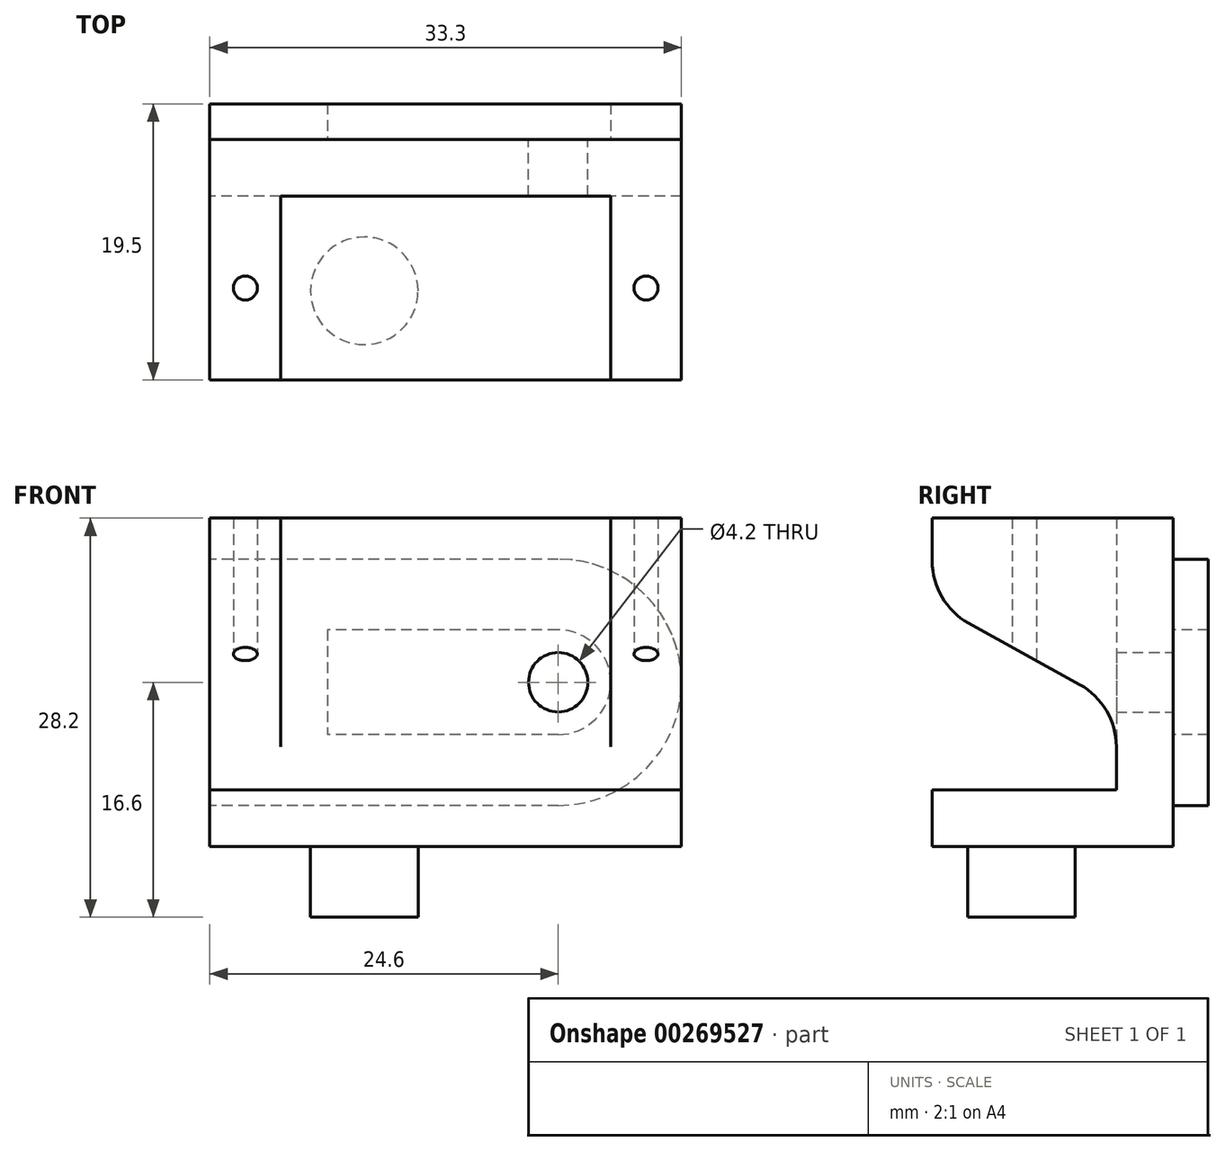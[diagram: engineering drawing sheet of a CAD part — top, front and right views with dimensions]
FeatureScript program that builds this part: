
annotation { "Feature Type Name" : "Feature", "Feature Type Description" : "" }
export const myFeature = defineFeature(function(context is Context, id is Id, definition is map)
    precondition{}
    {
        {
            var Q0;
            Q0=qCreatedBy(makeId("Top.planeOp"),FACE);
            var sketch = newSketch(context, id + "F0", { "sketchPlane" : qUnion([Q0])});
            skLineSegment(sketch, "E0.bottom", {"start": v(16.65, 8.5) * mm, "end": v(-16.65, 8.5) * mm});
            skLineSegment(sketch, "E0.top", {"start": v(16.65, -8.5) * mm, "end": v(-16.65, -8.5) * mm});
            skLineSegment(sketch, "E0.left", {"start": v(16.65, 8.5) * mm, "end": v(16.65, -8.5) * mm});
            skLineSegment(sketch, "E0.right", {"start": v(-16.65, 8.5) * mm, "end": v(-16.65, -8.5) * mm});
            skPoint(sketch, "E0.middle", {"position": v(0, 0) * mm});
            skLineSegment(sketch, "E1", {"start": v(11.65, -8.5) * mm, "end": v(11.65, 8.5) * mm});
            skLineSegment(sketch, "E2", {"start": v(-11.65, -8.5) * mm, "end": v(-11.65, 8.5) * mm});
            skLineSegment(sketch, "E3", {"start": v(-11.65, 4.5) * mm, "end": v(11.65, 4.5) * mm});
            skCircle(sketch, "E4", {"center": v(14.15, -2) * mm, "radius": 0.85 * mm});
            skCircle(sketch, "E5", {"center": v(-14.15, -2) * mm, "radius": 0.85 * mm});
            skCircle(sketch, "E6", {"center": v(-5.75, -2.2) * mm, "radius": 3.8 * mm});
            skCircle(sketch, "E7.MirrorC", {"center": v(5.75, -2.2) * mm, "radius": 3.8 * mm});
            skSolve(sketch);
        }
        {
            var Q0;
            Q0=qCreatedBy(makeId("Front.planeOp"),FACE);
            var sketch = newSketch(context, id + "F1", { "sketchPlane" : qUnion([Q0])});
            skLineSegment(sketch, "E8.bottom", {"start": v(-16.65, 0) * mm, "end": v(16.65, 0) * mm});
            skLineSegment(sketch, "E8.top", {"start": v(-16.65, 23.2) * mm, "end": v(16.65, 23.2) * mm});
            skLineSegment(sketch, "E8.left", {"start": v(-16.65, 0) * mm, "end": v(-16.65, 23.2) * mm});
            skLineSegment(sketch, "E8.right", {"start": v(16.65, 0) * mm, "end": v(16.65, 23.2) * mm});
            skLineSegment(sketch, "E9", {"start": v(-16.65, 4) * mm, "end": v(16.65, 4) * mm});
            skLineSegment(sketch, "E10", {"start": v(11.65, 0) * mm, "end": v(11.65, 23.2) * mm});
            skLineSegment(sketch, "E11", {"start": v(-11.65, 0) * mm, "end": v(-11.65, 23.2) * mm});
            skLineSegment(sketch, "E12", {"start": v(16.65, 10) * mm, "end": v(11.65, 10) * mm});
            skLineSegment(sketch, "E13", {"start": v(-11.65, 10) * mm, "end": v(-16.65, 10) * mm});
            skLineSegment(sketch, "E14", {"start": v(11.65, 17.2) * mm, "end": v(16.65, 17.2) * mm});
            skLineSegment(sketch, "E15", {"start": v(-11.65, 17.2) * mm, "end": v(-16.65, 17.2) * mm});
            skSolve(sketch);
        }
        {
            var Q0;
            Q0=qCreatedBy(makeId("Right.planeOp"),FACE);
            var sketch = newSketch(context, id + "F2", { "sketchPlane" : qUnion([Q0])});
            skLineSegment(sketch, "E16.bottom", {"start": v(-8.5, 0) * mm, "end": v(8.5, 0) * mm});
            skLineSegment(sketch, "E16.top", {"start": v(-8.5, 23.2) * mm, "end": v(8.5, 23.2) * mm});
            skLineSegment(sketch, "E16.left", {"start": v(-8.5, 20.15) * mm, "end": v(-8.5, 23.2) * mm});
            skLineSegment(sketch, "E16.right", {"start": v(8.5, 0) * mm, "end": v(8.5, 23.2) * mm});
            skLineSegment(sketch, "E17", {"start": v(4.5, 7.05) * mm, "end": v(4.5, 0) * mm});
            skLineSegment(sketch, "E18", {"start": v(4.5, 17.2) * mm, "end": v(-8.5, 17.2) * mm});
            skLineSegment(sketch, "E19", {"start": v(4.5, 4) * mm, "end": v(-8.5, 4) * mm});
            skLineSegment(sketch, "E20", {"start": v(-8.5, 10) * mm, "end": v(4.5, 10) * mm});
            skLineSegment(sketch, "E21", {"start": v(-5.92, 15.77) * mm, "end": v(1.92, 11.43) * mm});
            skArc(sketch, "E22.filletArc", {"start": v(-8.5, 20.15) * mm, "mid": v(-7.8, 17.6) * mm, "end": v(-5.92, 15.77) * mm});
            skArc(sketch, "E23.filletArc", {"start": v(4.5, 7.05) * mm, "mid": v(3.8, 9.6) * mm, "end": v(1.92, 11.43) * mm});
            skLineSegment(sketch, "E24", {"start": v(-8.5, 20.15) * mm, "end": v(-8.5, 0) * mm});
            skSolve(sketch);
        }
        {
            var Q0;
            {var subQ0=sQuery(id+"F1.wireOp",EDGE,"E13");Q0=makeQuery(id+"F1.imprint","IMPRINT",FACE,{"disambiguationData":[TD([[makeQuery(id+"F1.imprint","IMPRINT",EDGE,{"derivedFrom":subQ0}),-1.0]])]});}
            var Q1;
            {var subQ5=sQuery(id+"F1.wireOp",EDGE,"E15");Q1=makeQuery(id+"F1.imprint","IMPRINT",FACE,{"disambiguationData":[TD([[makeQuery(id+"F1.imprint","IMPRINT",EDGE,{"derivedFrom":subQ5}),-1.0]])]});}
            var Q2;
            {var subQ3=sQuery(id+"F1.wireOp",EDGE,"E13");Q2=makeQuery(id+"F1.imprint","IMPRINT",FACE,{"disambiguationData":[TD([[makeQuery(id+"F1.imprint","IMPRINT",EDGE,{"derivedFrom":subQ3}),1.0]])]});}
            var Q3;
            {var subQ0=sQuery(id+"F1.wireOp",EDGE,"E8.left");var subQ1=sQuery(id+"F1.wireOp",EDGE,"E8.bottom");var subQ2=makeQuery(id+"F1.imprint","INTERSECT",VERTEX,{"derivedFrom":[subQ1,subQ0]});Q3=makeQuery(id+"F1.imprint","IMPRINT",FACE,{"disambiguationData":[TD([[makeQuery(id+"F1.imprint","IMPRINT",EDGE,{"disambiguationData":[TD([[subQ2,-1.0]])],"derivedFrom":subQ1}),1.0]])]});}
            var Q4;
            {var subQ0=sQuery(id+"F1.wireOp",EDGE,"E10");var subQ1=sQuery(id+"F1.wireOp",EDGE,"E8.bottom");var subQ2=makeQuery(id+"F1.imprint","INTERSECT",VERTEX,{"derivedFrom":[subQ1,subQ0]});Q4=makeQuery(id+"F1.imprint","IMPRINT",FACE,{"disambiguationData":[TD([[makeQuery(id+"F1.imprint","IMPRINT",EDGE,{"disambiguationData":[TD([[subQ2,1.0]])],"derivedFrom":subQ1}),1.0]])]});}
            var Q5;
            {var subQ0=sQuery(id+"F1.wireOp",EDGE,"E8.right");var subQ1=sQuery(id+"F1.wireOp",EDGE,"E8.bottom");var subQ2=makeQuery(id+"F1.imprint","INTERSECT",VERTEX,{"derivedFrom":[subQ1,subQ0]});Q5=makeQuery(id+"F1.imprint","IMPRINT",FACE,{"disambiguationData":[TD([[makeQuery(id+"F1.imprint","IMPRINT",EDGE,{"disambiguationData":[TD([[subQ2,1.0]])],"derivedFrom":subQ1}),1.0]])]});}
            var Q6;
            {var subQ3=sQuery(id+"F1.wireOp",EDGE,"E12");Q6=makeQuery(id+"F1.imprint","IMPRINT",FACE,{"disambiguationData":[TD([[makeQuery(id+"F1.imprint","IMPRINT",EDGE,{"derivedFrom":subQ3}),1.0]])]});}
            var Q7;
            {var subQ0=sQuery(id+"F1.wireOp",EDGE,"E12");Q7=makeQuery(id+"F1.imprint","IMPRINT",FACE,{"disambiguationData":[TD([[makeQuery(id+"F1.imprint","IMPRINT",EDGE,{"derivedFrom":subQ0}),-1.0]])]});}
            var Q8;
            {var subQ5=sQuery(id+"F1.wireOp",EDGE,"E14");Q8=makeQuery(id+"F1.imprint","IMPRINT",FACE,{"disambiguationData":[TD([[makeQuery(id+"F1.imprint","IMPRINT",EDGE,{"derivedFrom":subQ5}),1.0]])]});}
            extrude(context, id + "F3", {"entities" : qUnion([Q0, Q1, Q2, Q3, Q4, Q5, Q6, Q7, Q8]), "endBound" : BoundingType.SYMMETRIC, "depth" : 17 * mm});
        }
        {
            var Q0;
            {var subQ5=sQuery(id+"F0.wireOp",EDGE,"E3");Q0=makeQuery(id+"F0.imprint","IMPRINT",FACE,{"disambiguationData":[TD([[makeQuery(id+"F0.imprint","IMPRINT",EDGE,{"derivedFrom":subQ5}),1.0]])]});}
            extrude(context, id + "F4", {"entities" : qUnion([Q0]), "operationType" : NewBodyOperationType.ADD, "depth" : 23.2 * mm});
        }
        {
            var Q0;
            {var subQ0=sQuery(id+"F2.wireOp",EDGE,"E21");Q0=makeQuery(id+"F2.imprint","IMPRINT",FACE,{"disambiguationData":[TD([[makeQuery(id+"F2.imprint","IMPRINT",EDGE,{"derivedFrom":subQ0}),-1.0]])]});}
            var Q1;
            {var subQ0=sQuery(id+"F2.wireOp",EDGE,"E24");var subQ1=sQuery(id+"F2.wireOp",EDGE,"E18");var subQ2=makeQuery(id+"F2.imprint","INTERSECT",VERTEX,{"derivedFrom":[subQ1,subQ0]});Q1=makeQuery(id+"F2.imprint","IMPRINT",FACE,{"disambiguationData":[TD([[makeQuery(id+"F2.imprint","IMPRINT",EDGE,{"disambiguationData":[TD([[subQ2,1.0]])],"derivedFrom":subQ1}),-1.0]])]});}
            var Q2;
            {var subQ5=sQuery(id+"F2.wireOp",EDGE,"E19");Q2=makeQuery(id+"F2.imprint","IMPRINT",FACE,{"disambiguationData":[TD([[makeQuery(id+"F2.imprint","IMPRINT",EDGE,{"derivedFrom":subQ5}),-1.0]])]});}
            extrude(context, id + "F5", {"entities" : qUnion([Q0, Q1, Q2]), "operationType" : NewBodyOperationType.REMOVE, "endBound" : BoundingType.SYMMETRIC, "oppositeDirection" : true, "depth" : 36.2 * mm});
        }
        {
            var Q0;
            Q0=makeQuery(id+"F0.imprint","IMPRINT",FACE,{"disambiguationData":[TD([[makeQuery(id+"F0.imprint","IMPRINT",EDGE,{"derivedFrom":sQuery(id+"F0.wireOp",EDGE,"E4")}),1.0]])]});
            var Q1;
            Q1=makeQuery(id+"F0.imprint","IMPRINT",FACE,{"disambiguationData":[TD([[makeQuery(id+"F0.imprint","IMPRINT",EDGE,{"derivedFrom":sQuery(id+"F0.wireOp",EDGE,"E5")}),1.0]])]});
            extrude(context, id + "F6", {"entities" : qUnion([Q0, Q1]), "operationType" : NewBodyOperationType.REMOVE, "depth" : 25 * mm, "hasSecondDirection" : true, "secondDirectionOppositeDirection" : false, "secondDirectionDepth" : 4.3 * mm});
        }
        {
            var Q0;
            Q0=makeQuery(id+"F0.imprint","IMPRINT",FACE,{"disambiguationData":[TD([[makeQuery(id+"F0.imprint","IMPRINT",EDGE,{"derivedFrom":sQuery(id+"F0.wireOp",EDGE,"E6")}),1.0]])]});
            extrude(context, id + "F7", {"entities" : qUnion([Q0]), "operationType" : NewBodyOperationType.ADD, "oppositeDirection" : true, "depth" : 5 * mm, "offsetDistance" : 25 * mm});
        }
        {
            var Q0;
            Q0=makeQuery(id+"F4.boolean.opBoolean","MERGE",FACE,{"derivedFrom":[makeQuery(id+"F3.opExtrude","CAP_FACE",FACE,{"disambiguationData":[OSD([sQuery(id+"F1.wireOp",EDGE,"E8.bottom"),sQuery(id+"F1.wireOp",EDGE,"E8.top"),sQuery(id+"F1.wireOp",EDGE,"E8.left"),sQuery(id+"F1.wireOp",EDGE,"E8.right"),sQuery(id+"F1.wireOp",EDGE,"E9"),sQuery(id+"F1.wireOp",EDGE,"E10"),sQuery(id+"F1.wireOp",EDGE,"E11")])],"isStart":true}),makeQuery(id+"F4.opExtrude","SWEPT_FACE",FACE,{"disambiguationData":[OSD([sQuery(id+"F0.wireOp",EDGE,"E0.bottom")])]})]});
            var sketch = newSketch(context, id + "F8", { "sketchPlane" : qUnion([Q0])});
            skLineSegment(sketch, "E25.bottom", {"start": v(-16.65, 0) * mm, "end": v(16.65, 0) * mm});
            skLineSegment(sketch, "E25.top", {"start": v(-16.65, 23.2) * mm, "end": v(16.65, 23.2) * mm});
            skLineSegment(sketch, "E25.left", {"start": v(-16.65, 0) * mm, "end": v(-16.65, 23.2) * mm});
            skLineSegment(sketch, "E25.right", {"start": v(16.65, 0) * mm, "end": v(16.65, 23.2) * mm});
            skCircle(sketch, "E26", {"center": v(-7.95, 11.6) * mm, "radius": 2.1 * mm});
            skCircle(sketch, "E27", {"center": v(-7.95, 11.6) * mm, "radius": 3.7 * mm});
            skLineSegment(sketch, "E28.bottom", {"start": v(-7.95, 15.3) * mm, "end": v(8.35, 15.3) * mm});
            skLineSegment(sketch, "E28.top", {"start": v(-7.95, 7.9) * mm, "end": v(8.35, 7.9) * mm});
            skLineSegment(sketch, "E28.left", {"start": v(-7.95, 15.3) * mm, "end": v(-7.95, 7.9) * mm});
            skLineSegment(sketch, "E28.right", {"start": v(8.35, 15.3) * mm, "end": v(8.35, 7.9) * mm});
            skCircle(sketch, "E29", {"center": v(-7.95, 11.6) * mm, "radius": 8.7 * mm});
            skLineSegment(sketch, "E30", {"start": v(-7.95, 20.3) * mm, "end": v(16.65, 20.3) * mm});
            skLineSegment(sketch, "E31", {"start": v(-7.95, 2.9) * mm, "end": v(16.65, 2.9) * mm});
            skSolve(sketch);
        }
        {
            var Q0;
            {var subQ4=sQuery(id+"F8.wireOp",EDGE,"E29");var subQ10=makeQuery(id+"F8.imprint","INTERSECT",VERTEX,{"derivedFrom":[subQ4,sQuery(id+"F8.wireOp",EDGE,"E30")]});Q0=makeQuery(id+"F8.imprint","IMPRINT",FACE,{"disambiguationData":[TD([[makeQuery(id+"F8.imprint","IMPRINT",EDGE,{"disambiguationData":[TD([[subQ10,1.0]])],"derivedFrom":subQ4}),1.0]])]});}
            var Q1;
            {var subQ0=sQuery(id+"F8.wireOp",EDGE,"E28.right");Q1=makeQuery(id+"F8.imprint","IMPRINT",FACE,{"disambiguationData":[TD([[makeQuery(id+"F8.imprint","IMPRINT",EDGE,{"derivedFrom":subQ0}),1.0]])]});}
            extrude(context, id + "F9", {"entities" : qUnion([Q0, Q1]), "operationType" : NewBodyOperationType.ADD, "depth" : 2.5 * mm, "offsetDistance" : 25 * mm});
        }
        {
            var Q0;
            {var subQ0=sQuery(id+"F8.wireOp",EDGE,"E28.left");var subQ1=sQuery(id+"F8.wireOp",EDGE,"E26");var subQ2=makeQuery(id+"F8.imprint","INTERSECT",VERTEX,{"disambiguationData":[OD(0.0)],"derivedFrom":[subQ1,subQ0]});Q0=makeQuery(id+"F8.imprint","IMPRINT",FACE,{"disambiguationData":[TD([[makeQuery(id+"F8.imprint","IMPRINT",EDGE,{"disambiguationData":[TD([[subQ2,1.0]])],"derivedFrom":subQ1}),1.0]])]});}
            var Q1;
            {var subQ0=sQuery(id+"F8.wireOp",EDGE,"E28.left");var subQ1=sQuery(id+"F8.wireOp",EDGE,"E26");var subQ2=makeQuery(id+"F8.imprint","INTERSECT",VERTEX,{"disambiguationData":[OD(0.0)],"derivedFrom":[subQ1,subQ0]});Q1=makeQuery(id+"F8.imprint","IMPRINT",FACE,{"disambiguationData":[TD([[makeQuery(id+"F8.imprint","IMPRINT",EDGE,{"disambiguationData":[TD([[subQ2,-1.0]])],"derivedFrom":subQ1}),1.0]])]});}
            extrude(context, id + "F10", {"entities" : qUnion([Q0, Q1]), "operationType" : NewBodyOperationType.REMOVE, "oppositeDirection" : true, "depth" : 27.6 * mm, "offsetDistance" : 25 * mm});
        }
    });
